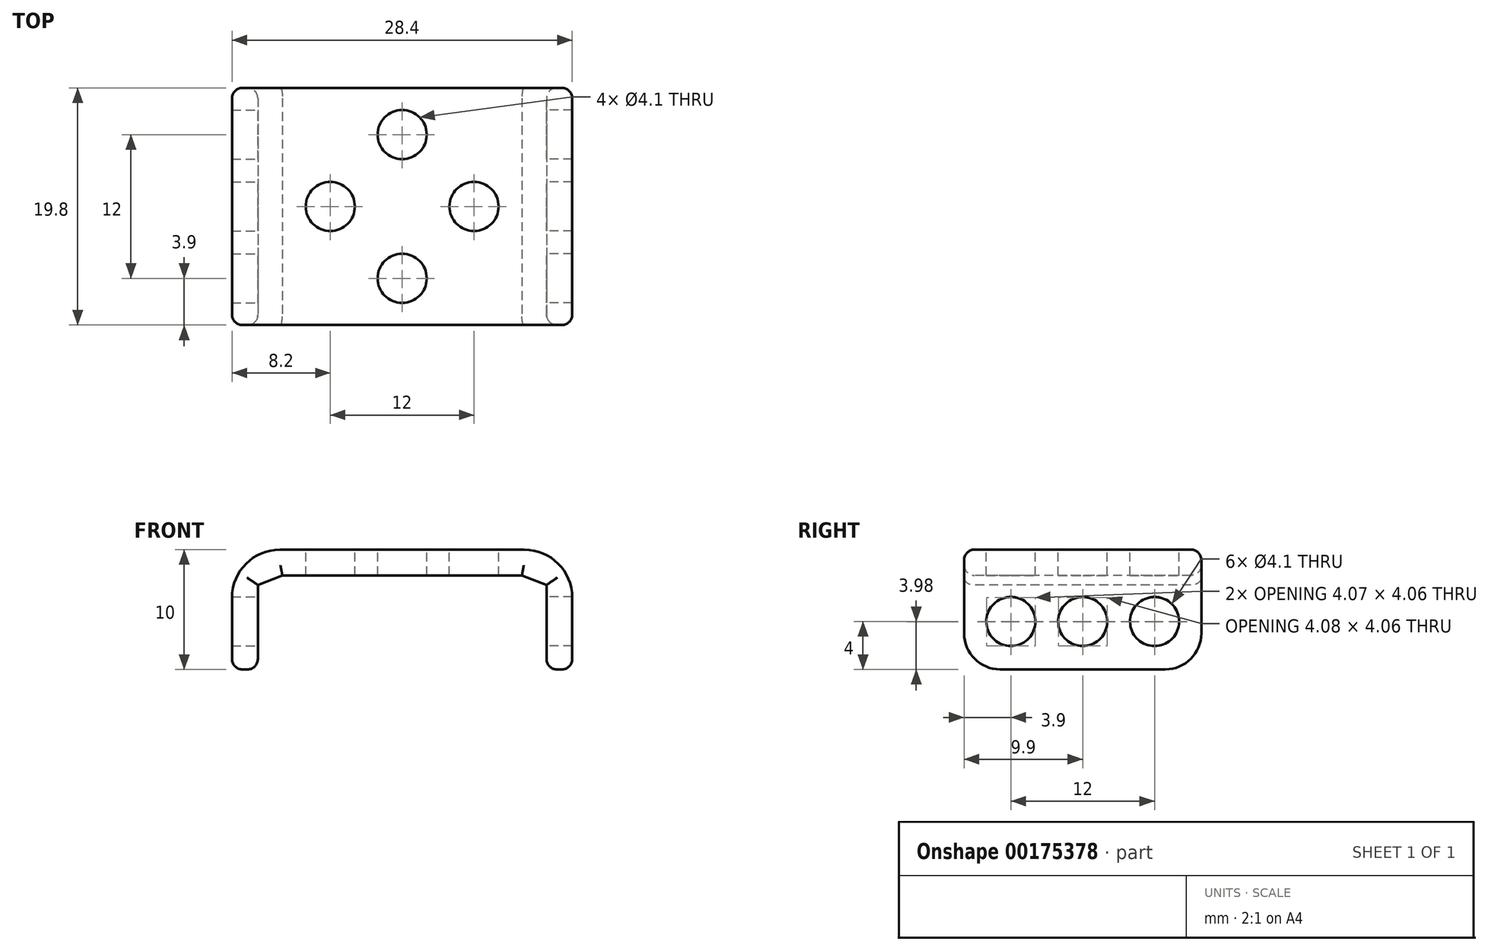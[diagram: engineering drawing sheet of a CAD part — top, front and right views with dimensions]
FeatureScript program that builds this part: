
annotation { "Feature Type Name" : "Feature", "Feature Type Description" : "" }
export const myFeature = defineFeature(function(context is Context, id is Id, definition is map)
    precondition{}
    {
        {
            assignVariable(context, id + "F0", {"name" : "printing_tolerance", "anyValue" : 0.05});
        }
        {
            assignVariable(context, id + "F1", {"name" : "thickness", "anyValue" : 2.2 - getVariable(context, 'printing_tolerance')});
        }
        {
            var Q0;
            Q0=qCreatedBy(makeId("Right.planeOp"),FACE);
            var sketch = newSketch(context, id + "F2", { "sketchPlane" : qUnion([Q0])});
            skPoint(sketch, "E0.center", {"position": v(0, 0) * mm});
            skLineSegment(sketch, "E1.rect.right", {"start": v(-12, -9) * mm, "end": v(-12, 27) * mm});
            skCircle(sketch, "E2", {"center": v(6, 24) * mm, "radius": 2 * mm});
            skLineSegment(sketch, "E3", {"start": v(0, 27) * mm, "end": v(0, -9) * mm, "construction": true});
            skCircle(sketch, "E4", {"center": v(0, 0) * mm, "radius": 8.9 * mm});
            skLineSegment(sketch, "E1.rect.left", {"start": v(12, -9) * mm, "end": v(12, 27) * mm});
            skLineSegment(sketch, "E1.rect.bottom", {"start": v(12, -9) * mm, "end": v(-12, -9) * mm});
            skLineSegment(sketch, "E1.rect.top", {"start": v(12, 27) * mm, "end": v(-12, 27) * mm});
            skLineSegment(sketch, "E5", {"start": v(-6, 24) * mm, "end": v(6, 24) * mm, "construction": true});
            skCircle(sketch, "E6", {"center": v(0, 24) * mm, "radius": 2 * mm});
            skPoint(sketch, "E1.rect.middle", {"position": v(0, 9) * mm});
            skCircle(sketch, "E0.2.0", {"center": v(0, -6) * mm, "radius": 2 * mm});
            skCircle(sketch, "E0.1.0", {"center": v(-6, 0) * mm, "radius": 2 * mm});
            skCircle(sketch, "E7", {"center": v(0, 0) * mm, "radius": 6 * mm, "construction": true});
            skCircle(sketch, "E8", {"center": v(0, 6) * mm, "radius": 2 * mm});
            skCircle(sketch, "E9", {"center": v(-4.24, 4.24) * mm, "radius": 0.8 * mm});
            skCircle(sketch, "E0.3.0", {"center": v(6, 0) * mm, "radius": 2 * mm});
            skCircle(sketch, "E10.3.0", {"center": v(4.24, 4.24) * mm, "radius": 0.8 * mm});
            skCircle(sketch, "E10.2.0", {"center": v(4.24, -4.24) * mm, "radius": 0.8 * mm});
            skCircle(sketch, "E10.1.0", {"center": v(-4.24, -4.24) * mm, "radius": 0.8 * mm});
            skCircle(sketch, "E11", {"center": v(-6, 24) * mm, "radius": 2 * mm});
            skPoint(sketch, "E12.orphan", {"position": v(-31.5, 36) * mm});
            skLineSegment(sketch, "E13.bottom", {"start": v(-27, 57) * mm, "end": v(9, 57) * mm});
            skLineSegment(sketch, "E13.top", {"start": v(-27, 33) * mm, "end": v(9, 33) * mm});
            skLineSegment(sketch, "E14", {"start": v(-27, 45) * mm, "end": v(9, 45) * mm, "construction": true});
            skLineSegment(sketch, "E13.left", {"start": v(9, 57) * mm, "end": v(9, 33) * mm});
            skLineSegment(sketch, "E15.bottom", {"start": v(-18, 51) * mm, "end": v(0, 51) * mm, "construction": true});
            skPoint(sketch, "E16.rect.left.start.orphan", {"position": v(-31.5, 54) * mm});
            skLineSegment(sketch, "E15.top", {"start": v(-18, 39) * mm, "end": v(0, 39) * mm, "construction": true});
            skLineSegment(sketch, "E15.left", {"start": v(-18, 51) * mm, "end": v(-18, 39) * mm, "construction": true});
            skLineSegment(sketch, "E15.right", {"start": v(0, 51) * mm, "end": v(0, 39) * mm, "construction": true});
            skLineSegment(sketch, "E16.rect.right", {"start": v(-22.5, 54) * mm, "end": v(-22.5, 36) * mm});
            skLineSegment(sketch, "E17.trimOffspring", {"start": v(-27, 36) * mm, "end": v(-27, 33) * mm});
            skLineSegment(sketch, "E16.rect.top", {"start": v(-22.5, 36) * mm, "end": v(-27, 36) * mm});
            skLineSegment(sketch, "E16.rect.bottom", {"start": v(-22.5, 54) * mm, "end": v(-27, 54) * mm});
            skCircle(sketch, "E18", {"center": v(-18, 51) * mm, "radius": 2 * mm});
            skCircle(sketch, "E19", {"center": v(-18, 39) * mm, "radius": 2 * mm});
            skCircle(sketch, "E20", {"center": v(0, 51) * mm, "radius": 2 * mm});
            skLineSegment(sketch, "E13.right", {"start": v(-27, 57) * mm, "end": v(-27, 54) * mm});
            skCircle(sketch, "E21", {"center": v(0, 39) * mm, "radius": 2 * mm});
            skLineSegment(sketch, "E22", {"start": v(0, 57) * mm, "end": v(0, 30) * mm, "construction": true});
            skLineSegment(sketch, "E23", {"start": v(-8.9, 30) * mm, "end": v(8.9, 30) * mm});
            skLineSegment(sketch, "E24", {"start": v(-8.9, 30) * mm, "end": v(-8.9, 33) * mm});
            skLineSegment(sketch, "E25", {"start": v(8.9, 30) * mm, "end": v(8.9, 33) * mm});
            skSolve(sketch);
        }
        {
            var Q0;
            Q0=qCreatedBy(makeId("Front.planeOp"),FACE);
            var sketch = newSketch(context, id + "F3", { "sketchPlane" : qUnion([Q0])});
            skLineSegment(sketch, "E26.MirrorCS", {"start": v(-12, -9) * mm, "end": v(0, -9) * mm});
            skLineSegment(sketch, "E27", {"start": v(15, 8.9) * mm, "end": v(15, -8.9) * mm});
            skLineSegment(sketch, "E28.MirrorCS", {"start": v(-12, 27) * mm, "end": v(-12, -9) * mm});
            skLineSegment(sketch, "E29", {"start": v(12, 27) * mm, "end": v(12, -9) * mm});
            skLineSegment(sketch, "E30", {"start": v(0, 22.5) * mm, "end": v(9, 22.5) * mm});
            skLineSegment(sketch, "E31.MirrorCS", {"start": v(0, 0) * mm, "end": v(-15, 0) * mm, "construction": true});
            skLineSegment(sketch, "E32.MirrorCS", {"start": v(0, 22.5) * mm, "end": v(-9, 22.5) * mm});
            skLineSegment(sketch, "E33.MirrorCS", {"start": v(-15, 8.9) * mm, "end": v(-15, -8.9) * mm});
            skLineSegment(sketch, "E34.MirrorCS", {"start": v(-9, 22.5) * mm, "end": v(-9, 27) * mm});
            skLineSegment(sketch, "E35", {"start": v(0, 47.92) * mm, "end": v(0, -10.42) * mm, "construction": true});
            skLineSegment(sketch, "E36", {"start": v(12, -9) * mm, "end": v(0, -9) * mm});
            skLineSegment(sketch, "E37", {"start": v(0, 0) * mm, "end": v(15, 0) * mm, "construction": true});
            skLineSegment(sketch, "E38.MirrorCS", {"start": v(-12, 8.9) * mm, "end": v(-15, 8.9) * mm});
            skLineSegment(sketch, "E39", {"start": v(12, 8.9) * mm, "end": v(15, 8.9) * mm});
            skLineSegment(sketch, "E40.MirrorCS", {"start": v(-15, -8.9) * mm, "end": v(-12, -8.9) * mm});
            skLineSegment(sketch, "E41", {"start": v(9, 27) * mm, "end": v(12, 27) * mm});
            skLineSegment(sketch, "E42", {"start": v(9, 22.5) * mm, "end": v(9, 27) * mm});
            skLineSegment(sketch, "E43.MirrorCS", {"start": v(-9, 27) * mm, "end": v(-12, 27) * mm});
            skLineSegment(sketch, "E44", {"start": v(15, -8.9) * mm, "end": v(12, -8.9) * mm});
            skSolve(sketch);
        }
        {
            var Q0;
            Q0=qCreatedBy(makeId("Top.planeOp"),FACE);
            var Q1;
            Q1=sQuery(id+"F2.wireOp",VERTEX,"E22.end");
            cPlane(context, id + "F4", {"entities" : qUnion([Q0, Q1]), "cplaneType" : CPlaneType.PLANE_POINT, "offset" : 150 * mm, "width" : 150 * mm, "height" : 150 * mm});
        }
        {
            var Q0;
            Q0=qCreatedBy(id+"F4.planeOp",FACE);
            var sketch = newSketch(context, id + "F5", { "sketchPlane" : qUnion([Q0])});
            skCircle(sketch, "E45", {"center": v(0, 0) * mm, "radius": 8.9 * mm});
            skCircle(sketch, "E46", {"center": v(0, 0) * mm, "radius": 6 * mm, "construction": true});
            skCircle(sketch, "E47", {"center": v(0, 6) * mm, "radius": 2 * mm});
            skCircle(sketch, "E48.1.0", {"center": v(-6, 0) * mm, "radius": 2 * mm});
            skCircle(sketch, "E48.2.0", {"center": v(0, -6) * mm, "radius": 2 * mm});
            skCircle(sketch, "E48.3.0", {"center": v(6, 0) * mm, "radius": 2 * mm});
            skSolve(sketch);
        }
        {
            var Q0;
            Q0=qCreatedBy(makeId("Right.planeOp"),FACE);
            var sketch = newSketch(context, id + "F6", { "sketchPlane" : qUnion([Q0])});
            skLineSegment(sketch, "E49.rect.bottom", {"start": v(6.9, 20) * mm, "end": v(-6.9, 20) * mm});
            skLineSegment(sketch, "E49.rect.top", {"start": v(9.9, 30) * mm, "end": v(-9.9, 30) * mm});
            skLineSegment(sketch, "E49.rect.left", {"start": v(9.9, 23) * mm, "end": v(9.9, 30) * mm});
            skLineSegment(sketch, "E49.rect.right", {"start": v(-9.9, 23) * mm, "end": v(-9.9, 30) * mm});
            skPoint(sketch, "E49.rect.middle", {"position": v(0, 25) * mm});
            skPoint(sketch, "E50.visualSharp", {"position": v(9.9, 20) * mm});
            skArc(sketch, "E50.filletArc", {"start": v(6.9, 20) * mm, "mid": v(9.02, 20.88) * mm, "end": v(9.9, 23) * mm});
            skPoint(sketch, "E51.visualSharp", {"position": v(-9.9, 20) * mm});
            skArc(sketch, "E51.filletArc", {"start": v(-9.9, 23) * mm, "mid": v(-9.02, 20.88) * mm, "end": v(-6.9, 20) * mm});
            skCircle(sketch, "E52", {"center": v(-6, 24) * mm, "radius": 2.05 * mm});
            skCircle(sketch, "E53", {"center": v(0, 24) * mm, "radius": 2.05 * mm});
            skCircle(sketch, "E54", {"center": v(6, 24) * mm, "radius": 2.05 * mm});
            skSolve(sketch);
        }
        {
            var Q0;
            Q0=qCreatedBy(makeId("Front.planeOp"),FACE);
            var sketch = newSketch(context, id + "F7", { "sketchPlane" : qUnion([Q0])});
            skLineSegment(sketch, "E55", {"start": v(0, 30) * mm, "end": v(10.2, 30) * mm});
            skLineSegment(sketch, "E56", {"start": v(14.2, 26) * mm, "end": v(14.2, 20) * mm});
            skLineSegment(sketch, "E57", {"start": v(14.2, 20) * mm, "end": v(12.05, 20) * mm});
            skLineSegment(sketch, "E58", {"start": v(12.05, 20) * mm, "end": v(12.05, 27.05) * mm});
            skLineSegment(sketch, "E59", {"start": v(12.05, 27.05) * mm, "end": v(10, 27.85) * mm});
            skLineSegment(sketch, "E60", {"start": v(10, 27.85) * mm, "end": v(0, 27.85) * mm});
            skLineSegment(sketch, "E61", {"start": v(0, 27.85) * mm, "end": v(0, 30) * mm});
            skPoint(sketch, "E62.visualSharp", {"position": v(14.2, 30) * mm});
            skArc(sketch, "E62.filletArc", {"start": v(14.2, 26) * mm, "mid": v(13.03, 28.83) * mm, "end": v(10.2, 30) * mm});
            skSolve(sketch);
        }
        {
            var Q0;
            Q0=makeQuery(id+"F6.imprint","IMPRINT",FACE,{"disambiguationData":[TD([[makeQuery(id+"F6.imprint","IMPRINT",EDGE,{"derivedFrom":sQuery(id+"F6.wireOp",EDGE,"E49.rect.bottom")}),-1.0]])]});
            extrude(context, id + "F8", {"entities" : qUnion([Q0]), "depth" : 25 * mm});
        }
        {
            var Q0;
            Q0=qSketchRegion(id+"F7",true);
            extrude(context, id + "F9", {"entities" : qUnion([Q0]), "operationType" : NewBodyOperationType.INTERSECT, "endBound" : BoundingType.THROUGH_ALL, "oppositeDirection" : true, "depth" : 25 * mm, "hasSecondDirection" : true, "secondDirectionBound" : SecondDirectionBoundingType.THROUGH_ALL, "secondDirectionOppositeDirection" : false, "secondDirectionDepth" : 25 * mm});
        }
        {
            var Q0;
            Q0=qCreatedBy(id+"F4.planeOp",FACE);
            var sketch = newSketch(context, id + "F10", { "sketchPlane" : qUnion([Q0])});
            skCircle(sketch, "E63", {"center": v(0, 0) * mm, "radius": 2.05 * mm, "construction": true});
            skCircle(sketch, "E64", {"center": v(0, 6) * mm, "radius": 2.05 * mm});
            skCircle(sketch, "E65", {"center": v(6, 0) * mm, "radius": 2.05 * mm});
            skCircle(sketch, "E66", {"center": v(0, -6) * mm, "radius": 2.05 * mm});
            skSolve(sketch);
        }
        {
            var Q0;
            Q0=qSketchRegion(id+"F10",true);
            extrude(context, id + "F11", {"entities" : qUnion([Q0]), "operationType" : NewBodyOperationType.REMOVE, "endBound" : BoundingType.THROUGH_ALL, "oppositeDirection" : true, "depth" : 25 * mm});
        }
        {
            var Q0;
            Q0=makeQuery(id+"F8.opExtrude","SWEPT_BODY",BODY,{"disambiguationData":[OSD([sQuery(id+"F6.wireOp",EDGE,"E49.rect.bottom"),sQuery(id+"F6.wireOp",EDGE,"E49.rect.top"),sQuery(id+"F6.wireOp",EDGE,"E49.rect.left"),sQuery(id+"F6.wireOp",EDGE,"E49.rect.right"),sQuery(id+"F6.wireOp",EDGE,"E50.filletArc"),sQuery(id+"F6.wireOp",EDGE,"E51.filletArc"),sQuery(id+"F6.wireOp",EDGE,"E52"),sQuery(id+"F6.wireOp",EDGE,"E53"),sQuery(id+"F6.wireOp",EDGE,"E54")])]});
            var Q1;
            Q1=qCreatedBy(makeId("Right.planeOp"),FACE);
            mirror(context, id + "F12", {"operationType" : NewBodyOperationType.ADD, "entities" : qUnion([Q0]), "mirrorPlane" : qUnion([Q1])});
        }
        {
            var Q0;
            {var subQ0=makeQuery(id+"F8.opExtrude","SWEPT_FACE",FACE,{"disambiguationData":[OSD([sQuery(id+"F6.wireOp",EDGE,"E49.rect.left")])]});Q0=makeQuery(id+"F12.boolean.opBoolean","MERGE",FACE,{"derivedFrom":[subQ0,makeQuery(id+"F12.opPattern","COPY",FACE,{"derivedFrom":subQ0,"instanceName":"1"})]});}
            var Q1;
            {var subQ0=makeQuery(id+"F8.opExtrude","SWEPT_FACE",FACE,{"disambiguationData":[OSD([sQuery(id+"F6.wireOp",EDGE,"E49.rect.right")])]});Q1=makeQuery(id+"F12.boolean.opBoolean","MERGE",FACE,{"derivedFrom":[subQ0,makeQuery(id+"F12.opPattern","COPY",FACE,{"derivedFrom":subQ0,"instanceName":"1"})]});}
            fillet(context, id + "F13", {"entities" : qUnion([Q0, Q1]), "radius" : (getVariable(context, 'thickness') / 2.5) * mm, "tangentPropagation" : true, "allowEdgeOverflow" : false});
        }
    });
